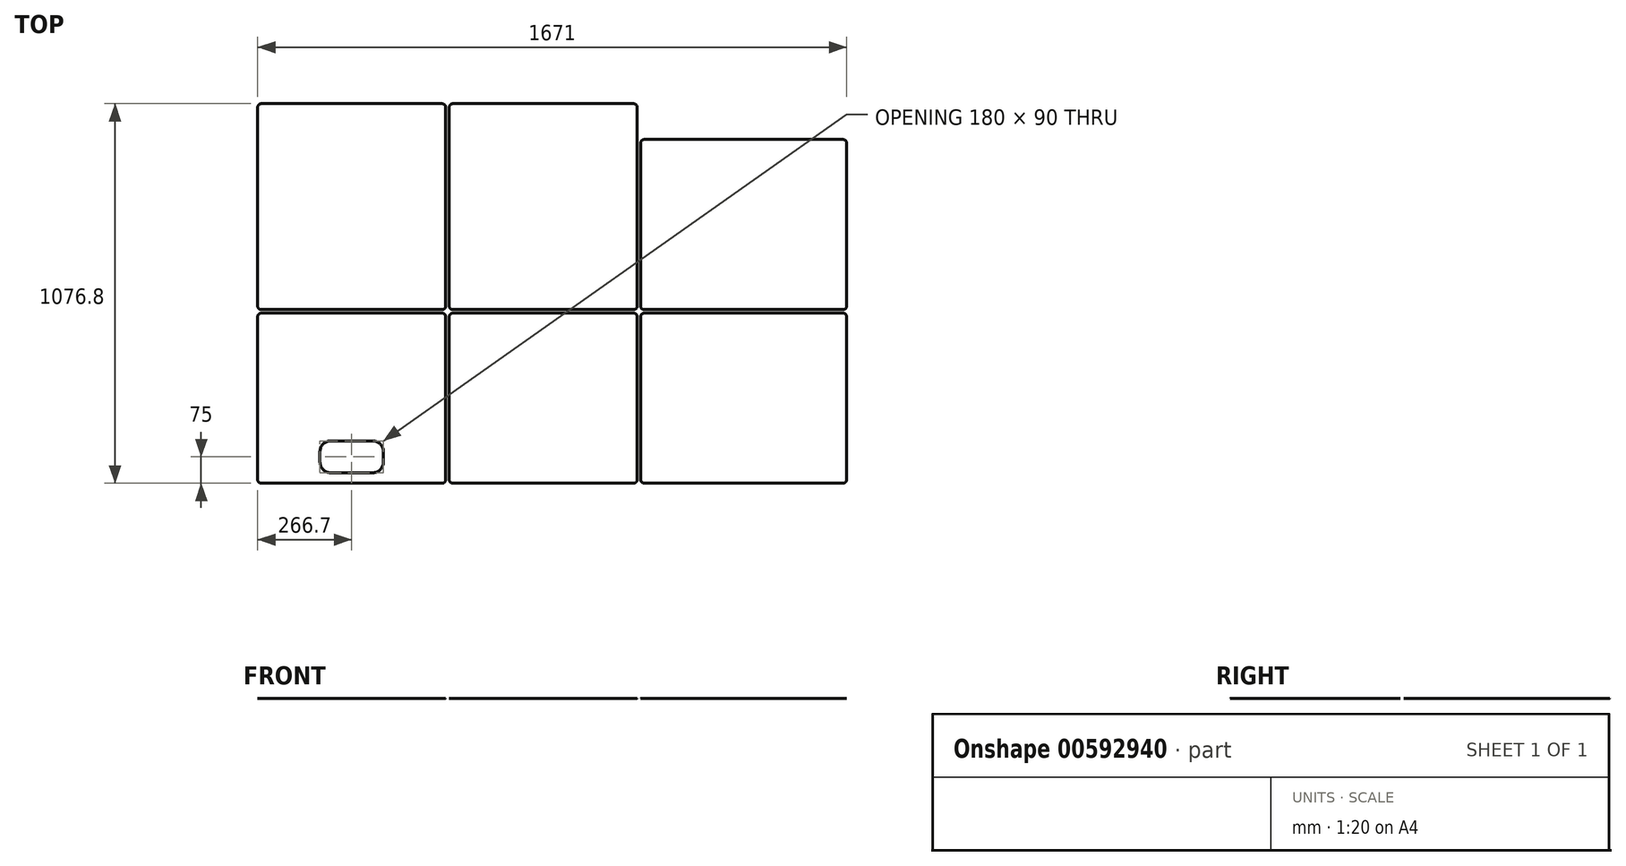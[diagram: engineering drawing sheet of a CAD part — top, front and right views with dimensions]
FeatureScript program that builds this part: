
annotation { "Feature Type Name" : "Feature", "Feature Type Description" : "" }
export const myFeature = defineFeature(function(context is Context, id is Id, definition is map)
    precondition{}
    {
        {
            var Q0;
            Q0=qCreatedBy(makeId("Top.planeOp"),FACE);
            var sketch = newSketch(context, id + "F0", { "sketchPlane" : qUnion([Q0])});
            skLineSegment(sketch, "E0.bottom", {"start": v(-523.4, 482.6) * mm, "end": v(-10, 482.6) * mm});
            skLineSegment(sketch, "E0.top", {"start": v(-523.4, 0) * mm, "end": v(-10, 0) * mm});
            skLineSegment(sketch, "E0.left", {"start": v(-533.4, 472.6) * mm, "end": v(-533.4, 10) * mm});
            skLineSegment(sketch, "E0.right", {"start": v(0, 472.6) * mm, "end": v(0, 10) * mm});
            skLineSegment(sketch, "E1.bottom", {"start": v(20, 482.6) * mm, "end": v(584.2, 482.6) * mm});
            skLineSegment(sketch, "E1.top", {"start": v(20, 0) * mm, "end": v(584.2, 0) * mm});
            skLineSegment(sketch, "E1.left", {"start": v(10, 472.6) * mm, "end": v(10, 10) * mm});
            skLineSegment(sketch, "E1.right", {"start": v(594.2, 472.6) * mm, "end": v(594.2, 10) * mm});
            skLineSegment(sketch, "E2.bottom", {"start": v(-523.4, 1076.8) * mm, "end": v(-10, 1076.8) * mm});
            skLineSegment(sketch, "E2.top", {"start": v(-523.4, 492.6) * mm, "end": v(-10, 492.6) * mm});
            skLineSegment(sketch, "E2.left", {"start": v(-533.4, 1066.8) * mm, "end": v(-533.4, 502.6) * mm});
            skLineSegment(sketch, "E2.right", {"start": v(0, 1066.8) * mm, "end": v(0, 502.6) * mm});
            skLineSegment(sketch, "E3.bottom", {"start": v(0, 0) * mm, "end": v(10, 0) * mm, "construction": true});
            skLineSegment(sketch, "E3.top", {"start": v(0, -10) * mm, "end": v(10, -10) * mm, "construction": true});
            skLineSegment(sketch, "E3.left", {"start": v(0, 0) * mm, "end": v(0, -10) * mm, "construction": true});
            skLineSegment(sketch, "E3.right", {"start": v(10, 0) * mm, "end": v(10, -10) * mm, "construction": true});
            skLineSegment(sketch, "E4.bottom", {"start": v(-543.4, 0) * mm, "end": v(-533.4, 0) * mm, "construction": true});
            skLineSegment(sketch, "E4.top", {"start": v(-543.4, -10) * mm, "end": v(-533.4, -10) * mm, "construction": true});
            skLineSegment(sketch, "E4.left", {"start": v(-543.4, 0) * mm, "end": v(-543.4, -10) * mm, "construction": true});
            skLineSegment(sketch, "E4.right", {"start": v(-533.4, 0) * mm, "end": v(-533.4, -10) * mm, "construction": true});
            skLineSegment(sketch, "E5.bottom", {"start": v(0, 482.6) * mm, "end": v(10, 482.6) * mm, "construction": true});
            skLineSegment(sketch, "E5.top", {"start": v(0, 492.6) * mm, "end": v(10, 492.6) * mm, "construction": true});
            skLineSegment(sketch, "E5.left", {"start": v(0, 482.6) * mm, "end": v(0, 492.6) * mm, "construction": true});
            skLineSegment(sketch, "E5.right", {"start": v(10, 482.6) * mm, "end": v(10, 492.6) * mm, "construction": true});
            skLineSegment(sketch, "E6.bottom", {"start": v(-553.4, 1076.8) * mm, "end": v(-1066.8, 1076.8) * mm});
            skLineSegment(sketch, "E6.top", {"start": v(-553.4, 492.6) * mm, "end": v(-1066.8, 492.6) * mm});
            skLineSegment(sketch, "E6.left", {"start": v(-543.4, 1066.8) * mm, "end": v(-543.4, 502.6) * mm});
            skLineSegment(sketch, "E6.right", {"start": v(-1076.8, 1066.8) * mm, "end": v(-1076.8, 502.6) * mm});
            skLineSegment(sketch, "E7.bottom", {"start": v(20, 492.6) * mm, "end": v(584.2, 492.6) * mm});
            skLineSegment(sketch, "E7.top", {"start": v(20, 975.2) * mm, "end": v(584.2, 975.2) * mm});
            skLineSegment(sketch, "E7.left", {"start": v(10, 502.6) * mm, "end": v(10, 965.2) * mm});
            skLineSegment(sketch, "E7.right", {"start": v(594.2, 502.6) * mm, "end": v(594.2, 965.2) * mm});
            skLineSegment(sketch, "E8.bottom", {"start": v(-553.4, 0) * mm, "end": v(-1066.8, 0) * mm});
            skLineSegment(sketch, "E8.top", {"start": v(-553.4, 482.6) * mm, "end": v(-1066.8, 482.6) * mm});
            skLineSegment(sketch, "E8.left", {"start": v(-543.4, 10) * mm, "end": v(-543.4, 472.6) * mm});
            skLineSegment(sketch, "E8.right", {"start": v(-1076.8, 10) * mm, "end": v(-1076.8, 472.6) * mm});
            skLineSegment(sketch, "E9.bottom", {"start": v(-870.1, 120) * mm, "end": v(-750.1, 120) * mm});
            skLineSegment(sketch, "E9.top", {"start": v(-870.1, 30) * mm, "end": v(-750.1, 30) * mm});
            skLineSegment(sketch, "E9.left", {"start": v(-900.1, 90) * mm, "end": v(-900.1, 60) * mm});
            skLineSegment(sketch, "E9.right", {"start": v(-720.1, 90) * mm, "end": v(-720.1, 60) * mm});
            skPoint(sketch, "E10", {"position": v(-810.1, 120) * mm});
            skPoint(sketch, "E11", {"position": v(-810.1, 482.6) * mm});
            skPoint(sketch, "E12.visualSharp", {"position": v(-1076.8, 1076.8) * mm});
            skArc(sketch, "E12.filletArc", {"start": v(-1066.8, 1076.8) * mm, "mid": v(-1073.87, 1073.87) * mm, "end": v(-1076.8, 1066.8) * mm});
            skPoint(sketch, "E13.visualSharp", {"position": v(-543.4, 1076.8) * mm});
            skArc(sketch, "E13.filletArc", {"start": v(-543.4, 1066.8) * mm, "mid": v(-546.33, 1073.87) * mm, "end": v(-553.4, 1076.8) * mm});
            skPoint(sketch, "E14.visualSharp", {"position": v(-533.4, 1076.8) * mm});
            skArc(sketch, "E14.filletArc", {"start": v(-523.4, 1076.8) * mm, "mid": v(-530.47, 1073.87) * mm, "end": v(-533.4, 1066.8) * mm});
            skPoint(sketch, "E15.visualSharp", {"position": v(-1076.8, 492.6) * mm});
            skArc(sketch, "E15.filletArc", {"start": v(-1076.8, 502.6) * mm, "mid": v(-1073.87, 495.53) * mm, "end": v(-1066.8, 492.6) * mm});
            skPoint(sketch, "E16.visualSharp", {"position": v(-543.4, 492.6) * mm});
            skArc(sketch, "E16.filletArc", {"start": v(-553.4, 492.6) * mm, "mid": v(-546.33, 495.53) * mm, "end": v(-543.4, 502.6) * mm});
            skPoint(sketch, "E17.visualSharp", {"position": v(0, 1076.8) * mm});
            skArc(sketch, "E17.filletArc", {"start": v(0, 1066.8) * mm, "mid": v(-2.93, 1073.87) * mm, "end": v(-10, 1076.8) * mm});
            skPoint(sketch, "E18.visualSharp", {"position": v(0, 492.6) * mm});
            skArc(sketch, "E18.filletArc", {"start": v(-10, 492.6) * mm, "mid": v(-2.93, 495.53) * mm, "end": v(0, 502.6) * mm});
            skPoint(sketch, "E19.visualSharp", {"position": v(-533.4, 492.6) * mm});
            skArc(sketch, "E19.filletArc", {"start": v(-533.4, 502.6) * mm, "mid": v(-530.47, 495.53) * mm, "end": v(-523.4, 492.6) * mm});
            skPoint(sketch, "E20.visualSharp", {"position": v(-533.4, 482.6) * mm});
            skArc(sketch, "E20.filletArc", {"start": v(-523.4, 482.6) * mm, "mid": v(-530.47, 479.67) * mm, "end": v(-533.4, 472.6) * mm});
            skPoint(sketch, "E21.visualSharp", {"position": v(0, 482.6) * mm});
            skArc(sketch, "E21.filletArc", {"start": v(0, 472.6) * mm, "mid": v(-2.93, 479.67) * mm, "end": v(-10, 482.6) * mm});
            skPoint(sketch, "E22.visualSharp", {"position": v(-1076.8, 482.6) * mm});
            skArc(sketch, "E22.filletArc", {"start": v(-1066.8, 482.6) * mm, "mid": v(-1073.87, 479.67) * mm, "end": v(-1076.8, 472.6) * mm});
            skPoint(sketch, "E23.visualSharp", {"position": v(-543.4, 482.6) * mm});
            skArc(sketch, "E23.filletArc", {"start": v(-543.4, 472.6) * mm, "mid": v(-546.33, 479.67) * mm, "end": v(-553.4, 482.6) * mm});
            skPoint(sketch, "E24.visualSharp", {"position": v(10, 975.2) * mm});
            skArc(sketch, "E24.filletArc", {"start": v(20, 975.2) * mm, "mid": v(12.93, 972.27) * mm, "end": v(10, 965.2) * mm});
            skPoint(sketch, "E25.visualSharp", {"position": v(594.2, 975.2) * mm});
            skArc(sketch, "E25.filletArc", {"start": v(594.2, 965.2) * mm, "mid": v(591.27, 972.27) * mm, "end": v(584.2, 975.2) * mm});
            skPoint(sketch, "E26.visualSharp", {"position": v(10, 492.6) * mm});
            skArc(sketch, "E26.filletArc", {"start": v(10, 502.6) * mm, "mid": v(12.93, 495.53) * mm, "end": v(20, 492.6) * mm});
            skPoint(sketch, "E27.visualSharp", {"position": v(594.2, 492.6) * mm});
            skArc(sketch, "E27.filletArc", {"start": v(584.2, 492.6) * mm, "mid": v(591.27, 495.53) * mm, "end": v(594.2, 502.6) * mm});
            skPoint(sketch, "E28.visualSharp", {"position": v(594.2, 0) * mm});
            skArc(sketch, "E28.filletArc", {"start": v(584.2, 0) * mm, "mid": v(591.27, 2.93) * mm, "end": v(594.2, 10) * mm});
            skPoint(sketch, "E29.visualSharp", {"position": v(594.2, 482.6) * mm});
            skArc(sketch, "E29.filletArc", {"start": v(594.2, 472.6) * mm, "mid": v(591.27, 479.67) * mm, "end": v(584.2, 482.6) * mm});
            skPoint(sketch, "E30.visualSharp", {"position": v(10, 0) * mm});
            skArc(sketch, "E30.filletArc", {"start": v(10, 10) * mm, "mid": v(12.93, 2.93) * mm, "end": v(20, 0) * mm});
            skPoint(sketch, "E31.visualSharp", {"position": v(10, 482.6) * mm});
            skArc(sketch, "E31.filletArc", {"start": v(20, 482.6) * mm, "mid": v(12.93, 479.67) * mm, "end": v(10, 472.6) * mm});
            skPoint(sketch, "E32.visualSharp", {"position": v(-1076.8, 0) * mm});
            skArc(sketch, "E32.filletArc", {"start": v(-1076.8, 10) * mm, "mid": v(-1073.87, 2.93) * mm, "end": v(-1066.8, 0) * mm});
            skPoint(sketch, "E33.visualSharp", {"position": v(-543.4, 0) * mm});
            skArc(sketch, "E33.filletArc", {"start": v(-553.4, 0) * mm, "mid": v(-546.33, 2.93) * mm, "end": v(-543.4, 10) * mm});
            skPoint(sketch, "E34.visualSharp", {"position": v(-533.4, 0) * mm});
            skArc(sketch, "E34.filletArc", {"start": v(-533.4, 10) * mm, "mid": v(-530.47, 2.93) * mm, "end": v(-523.4, 0) * mm});
            skPoint(sketch, "E35.visualSharp", {"position": v(0, 0) * mm});
            skArc(sketch, "E35.filletArc", {"start": v(-10, 0) * mm, "mid": v(-2.93, 2.93) * mm, "end": v(0, 10) * mm});
            skPoint(sketch, "E36.visualSharp", {"position": v(-720.1, 120) * mm});
            skArc(sketch, "E36.filletArc", {"start": v(-720.1, 90) * mm, "mid": v(-728.89, 111.21) * mm, "end": v(-750.1, 120) * mm});
            skPoint(sketch, "E37.visualSharp", {"position": v(-720.1, 30) * mm});
            skArc(sketch, "E37.filletArc", {"start": v(-750.1, 30) * mm, "mid": v(-728.89, 38.79) * mm, "end": v(-720.1, 60) * mm});
            skPoint(sketch, "E38.visualSharp", {"position": v(-900.1, 30) * mm});
            skArc(sketch, "E38.filletArc", {"start": v(-900.1, 60) * mm, "mid": v(-891.31, 38.79) * mm, "end": v(-870.1, 30) * mm});
            skPoint(sketch, "E39.visualSharp", {"position": v(-900.1, 120) * mm});
            skArc(sketch, "E39.filletArc", {"start": v(-870.1, 120) * mm, "mid": v(-891.31, 111.21) * mm, "end": v(-900.1, 90) * mm});
            skLineSegment(sketch, "E40.bottom", {"start": v(185.63, 1057.4) * mm, "end": v(211.03, 1057.4) * mm});
            skLineSegment(sketch, "E40.top", {"start": v(185.63, 1032) * mm, "end": v(211.03, 1032) * mm});
            skLineSegment(sketch, "E40.left", {"start": v(185.63, 1057.4) * mm, "end": v(185.63, 1032) * mm});
            skLineSegment(sketch, "E40.right", {"start": v(211.03, 1057.4) * mm, "end": v(211.03, 1032) * mm});
            skText(sketch, "E41", { "text": "one inch square", "fontName": "OpenSans-Regular.ttf"});
            const initialGuessF0  = {"E41": [0.15099, 1.01534, 1, 0, 0.0096]};
            skSetInitialGuess(sketch, initialGuessF0);
            skSolve(sketch);
        }
        {
            var Q0;
            Q0=makeQuery(id+"F0.imprint","IMPRINT",FACE,{"disambiguationData":[TD([[makeQuery(id+"F0.imprint","IMPRINT",EDGE,{"derivedFrom":sQuery(id+"F0.wireOp",EDGE,"E2.bottom")}),-1.0]])]});
            var Q1;
            Q1=makeQuery(id+"F0.imprint","IMPRINT",FACE,{"disambiguationData":[TD([[makeQuery(id+"F0.imprint","IMPRINT",EDGE,{"derivedFrom":sQuery(id+"F0.wireOp",EDGE,"E0.bottom")}),-1.0]])]});
            var Q2;
            Q2=makeQuery(id+"F0.imprint","IMPRINT",FACE,{"disambiguationData":[TD([[makeQuery(id+"F0.imprint","IMPRINT",EDGE,{"derivedFrom":sQuery(id+"F0.wireOp",EDGE,"E1.bottom")}),-1.0]])]});
            var Q3;
            Q3=makeQuery(id+"F0.imprint","IMPRINT",FACE,{"disambiguationData":[TD([[makeQuery(id+"F0.imprint","IMPRINT",EDGE,{"derivedFrom":sQuery(id+"F0.wireOp",EDGE,"qb5XeDrG-2hPw-eqVY-Hkqy-UkKiLDwqCIfb.bottom")}),-1.0]])]});
            var Q4;
            Q4=makeQuery(id+"F0.imprint","IMPRINT",FACE,{"disambiguationData":[TD([[makeQuery(id+"F0.imprint","IMPRINT",EDGE,{"derivedFrom":sQuery(id+"F0.wireOp",EDGE,"OFzEOZim-rscy-FU7G-CVIq-rmkUErnIfepD.bottom")}),1.0]])]});
            var Q5;
            Q5=makeQuery(id+"F0.imprint","IMPRINT",FACE,{"disambiguationData":[TD([[makeQuery(id+"F0.imprint","IMPRINT",EDGE,{"derivedFrom":sQuery(id+"F0.wireOp",EDGE,"E6.bottom")}),1.0]])]});
            var Q6;
            Q6=makeQuery(id+"F0.imprint","IMPRINT",FACE,{"disambiguationData":[TD([[makeQuery(id+"F0.imprint","IMPRINT",EDGE,{"derivedFrom":sQuery(id+"F0.wireOp",EDGE,"E8.bottom")}),-1.0]])]});
            var Q7;
            Q7=makeQuery(id+"F0.imprint","IMPRINT",FACE,{"disambiguationData":[TD([[makeQuery(id+"F0.imprint","IMPRINT",EDGE,{"derivedFrom":sQuery(id+"F0.wireOp",EDGE,"E7.bottom")}),1.0]])]});
            var Q8;
            {var subQ3=sQuery(id+"F0.wireOp",EDGE,"bcbc3ae7-48da-4cd3-98e6-b9f1b75fc4c6");Q8=makeQuery(id+"F0.imprint","IMPRINT",FACE,{"disambiguationData":[TD([[makeQuery(id+"F0.imprint","IMPRINT",EDGE,{"derivedFrom":subQ3}),1.0]])]});}
            var Q9;
            {var subQ3=sQuery(id+"F0.wireOp",EDGE,"6285c4a6-4117-4368-b7bf-b7f88f4e9073");Q9=makeQuery(id+"F0.imprint","IMPRINT",FACE,{"disambiguationData":[TD([[makeQuery(id+"F0.imprint","IMPRINT",EDGE,{"derivedFrom":subQ3}),1.0]])]});}
            var Q10;
            {var subQ3=sQuery(id+"F0.wireOp",EDGE,"c186329f-ecbe-4744-ade4-a3b3c9fb7db8");Q10=makeQuery(id+"F0.imprint","IMPRINT",FACE,{"disambiguationData":[TD([[makeQuery(id+"F0.imprint","IMPRINT",EDGE,{"derivedFrom":subQ3}),-1.0]])]});}
            var Q11;
            {var subQ3=sQuery(id+"F0.wireOp",EDGE,"00d3c42e-ecfa-4a4a-8300-ccc4e2d1fe89");Q11=makeQuery(id+"F0.imprint","IMPRINT",FACE,{"disambiguationData":[TD([[makeQuery(id+"F0.imprint","IMPRINT",EDGE,{"derivedFrom":subQ3}),1.0]])]});}
            extrude(context, id + "F1", {"entities" : qUnion([Q0, Q1, Q2, Q3, Q4, Q5, Q6, Q7, Q8, Q9, Q10, Q11]), "depth" : 1 / 203.2 * mm, "offsetDistance" : 25 * mm});
        }
    });
